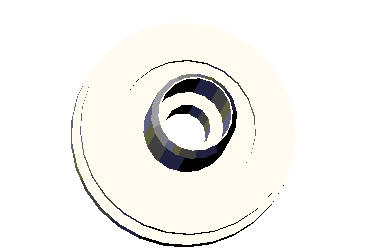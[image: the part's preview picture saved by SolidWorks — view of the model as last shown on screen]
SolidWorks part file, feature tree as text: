
SOLIDWORKS PART (.sldprt)
format: sldprt  version: not decoded by parser v0  size: 352,256 bytes
history: native  units: mm
features: sketch x12, extrude x7, cut_extrude x5, plane x4, chamfer x1 + 1 further entry (+6 scaffold rows collapsed)
feature tree (36):
  scaffold x6  (default folders/planes/origin — collapsed)
  "Corps de surface"
  plane  "Plan1"
  plane  "Plan2"
  plane  "Plan3"
  sketch  "Esquisse1"  dims[D1=78.0mm]
  extrude  "Base-Extrusion"  Depth=3mm
  sketch  "Esquisse2"  dims[D1=78.0mm D2=77.0mm]
  extrude  "Boss.-Extru.1"  Depth=3mm
  sketch  "Esquisse3"  dims[D1=60.0mm]
  extrude  "Boss.-Extru.2"  Depth=10mm
  sketch  "Esquisse4"  dims[D1=74.0mm]
  extrude  "Boss.-Extru.3"  Depth=3mm
  sketch  "Esquisse5"  dims[D1=48.0mm]
  cut_extrude  "Enlèv. mat.-Extru.1"  Depth=3mm
  sketch  "Esquisse6"  dims[D1=30.0mm]
  extrude  "Boss.-Extru.4"  Depth=38mm
  sketch  "Esquisse7"  dims[D1=25.0mm]
  cut_extrude  "Enlèv. mat.-Extru.2"  Depth=33mm
  chamfer  "Chanfrein2"  Distance=6mm
  sketch  "Esquisse11"  dims[D1=55.0mm]
  cut_extrude  "Enlèv. mat.-Extru.8"  Depth=7mm
  sketch  "Esquisse12"  dims[D1=25.0mm]
  extrude  "Boss.-Extru.5"  Depth=10mm
  plane  "Plan4"  Offset=3mm
  sketch  "Esquisse13"  dims[D1=1.5mm D2=11.0mm D3=34.0mm D4=3.0mm]
  extrude  "Boss.-Extru.6"  [1 undecoded]
  sketch  "Esquisse18"  dims[D1=16.0mm]
  cut_extrude  "Enlèv. mat.-Extru.11"  [1 undecoded]
  sketch  "Esquisse19"  dims[D1=1.5mm]
  cut_extrude  "Enlèv. mat.-Extru.12"  Depth=1mm
decode coverage: 23 of 25 modeling features carry decoded parameters; 1 rows unclassified (native names shown)
note: 2 parameter values undecoded
note: suppression state not decoded; provenance and decode notes live in map.json
